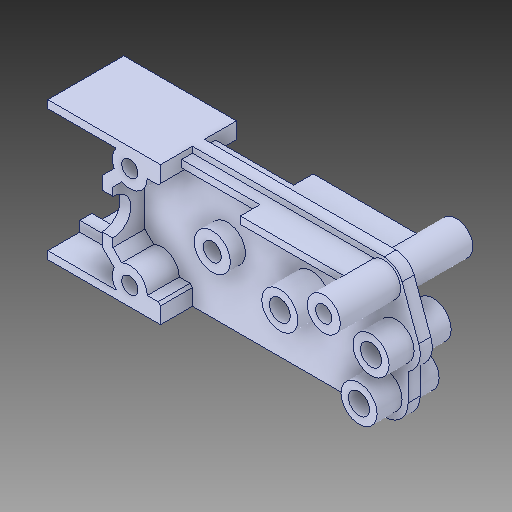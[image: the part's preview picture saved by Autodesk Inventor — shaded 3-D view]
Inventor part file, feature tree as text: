
AUTODESK INVENTOR PART (.ipt)
format: ipt  version: 2019.1 (Build 231200000, 200)  size: 243,200 bytes
history: mixed  units: in
note: dims shown in document units (in); Inventor stores cm internally (conversion verified against a paired STEP export)
features: chamfer x1, imported_body x1
ambient origin geometry x8: Origin, YZ Plane, XZ Plane, XY Plane, X Axis, Y Axis, Z Axis, Center Point
bodies: Solid1 (imported_parasolid)
feature tree (2):
  chamfer  "Chamfer2"  [1 undecoded]
  imported_body  NMx_Import_Brep_tag  [imported B-rep: ~95 faces, bbox_mm=[56.256781, 23.0, 22.0]]
note: 1 required parameter value undecoded (feature->parameter linkage not recoverable at this tier; creation-order binding heuristic only, values carry confidence <= 0.55)
